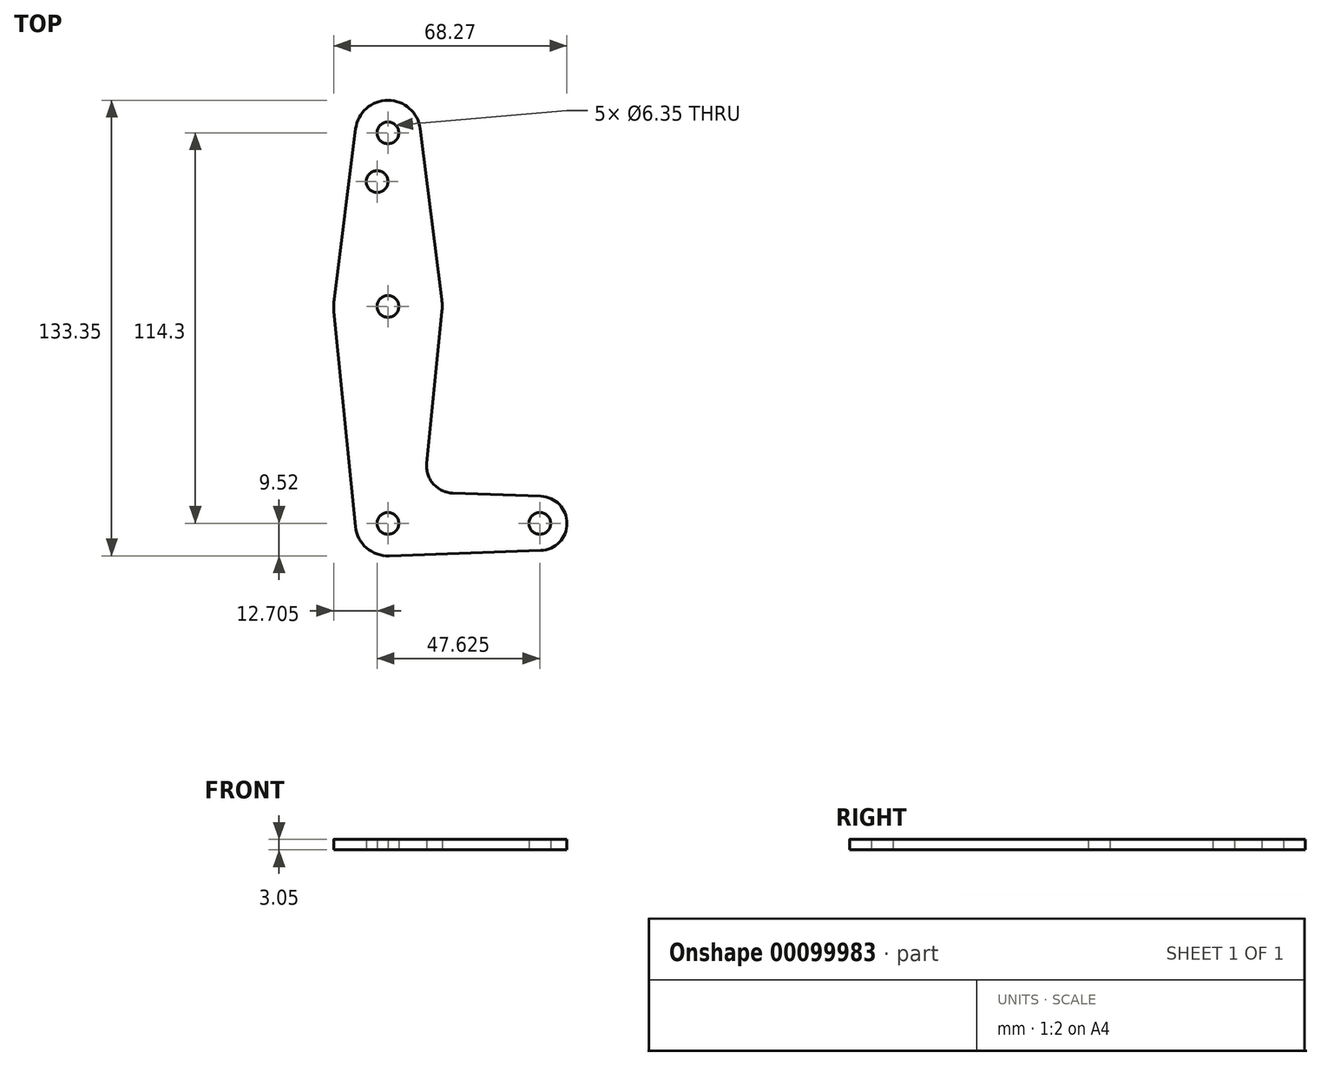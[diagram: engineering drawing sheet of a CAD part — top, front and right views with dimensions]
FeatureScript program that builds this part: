
annotation { "Feature Type Name" : "Feature", "Feature Type Description" : "" }
export const myFeature = defineFeature(function(context is Context, id is Id, definition is map)
    precondition{}
    {
        {
            var Q0;
            Q0=qCreatedBy(makeId("Top.planeOp"),FACE);
            var sketch = newSketch(context, id + "F0", { "sketchPlane" : qUnion([Q0])});
            skLineSegment(sketch, "E0", {"start": v(0, 114.3) * mm, "end": v(0, 0) * mm, "construction": true});
            skLineSegment(sketch, "E1", {"start": v(0, 0) * mm, "end": v(44.45, 0) * mm, "construction": true});
            skCircle(sketch, "E2", {"center": v(0, 114.3) * mm, "radius": 9.53 * mm});
            skCircle(sketch, "E3", {"center": v(0, 0) * mm, "radius": 9.53 * mm});
            skCircle(sketch, "E4", {"center": v(44.45, 0) * mm, "radius": 7.94 * mm});
            skCircle(sketch, "E5", {"center": v(0, 63.5) * mm, "radius": 15.88 * mm});
            skLineSegment(sketch, "E6", {"start": v(0, 63.5) * mm, "end": v(0, 0) * mm, "construction": true});
            skLineSegment(sketch, "E7", {"start": v(-15.75, 65.48) * mm, "end": v(-9.45, 115.5) * mm});
            skLineSegment(sketch, "E8", {"start": v(9.45, 115.5) * mm, "end": v(15.75, 65.48) * mm});
            skCircle(sketch, "E9", {"center": v(0, 114.3) * mm, "radius": 3.18 * mm});
            skCircle(sketch, "E10", {"center": v(0, 63.5) * mm, "radius": 3.18 * mm});
            skCircle(sketch, "E11", {"center": v(0, 0) * mm, "radius": 3.18 * mm});
            skCircle(sketch, "E12", {"center": v(44.45, 0) * mm, "radius": 3.18 * mm});
            skCircle(sketch, "E13", {"center": v(-3.17, 100.03) * mm, "radius": 3.18 * mm});
            skLineSegment(sketch, "E14", {"start": v(-15.8, 61.91) * mm, "end": v(-9.48, -0.95) * mm});
            skLineSegment(sketch, "E15", {"start": v(15.8, 61.91) * mm, "end": v(11.34, 17.6) * mm});
            skLineSegment(sketch, "E16", {"start": v(18.97, 8.85) * mm, "end": v(44.73, 7.93) * mm});
            skLineSegment(sketch, "E17", {"start": v(0.34, -9.52) * mm, "end": v(44.73, -7.93) * mm});
            skArc(sketch, "E18.filletArc", {"start": v(11.34, 17.6) * mm, "mid": v(13.26, 11.57) * mm, "end": v(18.97, 8.85) * mm});
            skSolve(sketch);
        }
        {
            var Q0;
            Q0 = qSketchRegion(id + "F0", true);
            extrude(context, id + "F1", {"entities" : qUnion([Q0]), "depth" : 3.05 * mm});
        }
    });
